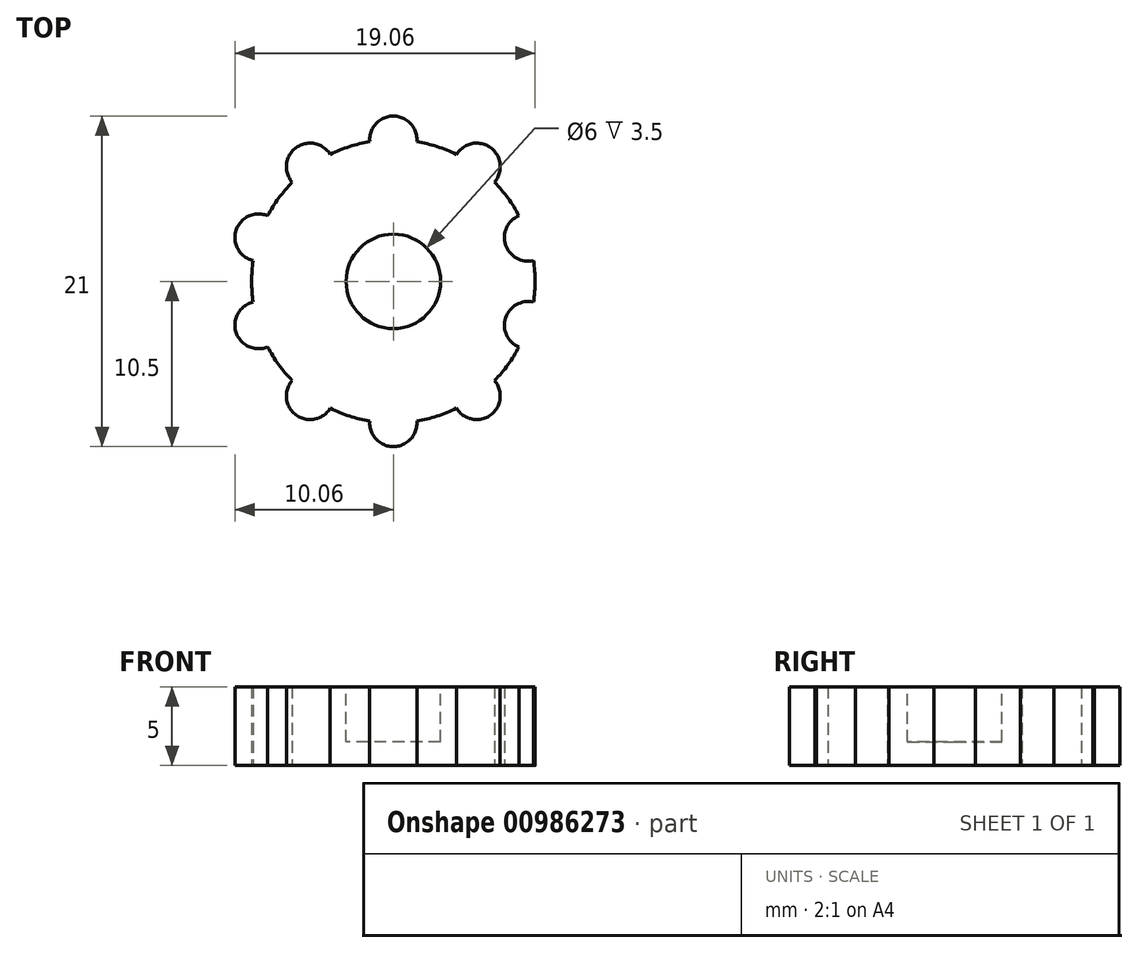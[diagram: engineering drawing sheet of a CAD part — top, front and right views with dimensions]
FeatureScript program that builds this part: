
annotation { "Feature Type Name" : "Feature", "Feature Type Description" : "" }
export const myFeature = defineFeature(function(context is Context, id is Id, definition is map)
    precondition{}
    {
        {
            var Q0;
            Q0=qCreatedBy(makeId("Top.planeOp"),FACE);
            var sketch = newSketch(context, id + "F0", { "sketchPlane" : qUnion([Q0])});
            skCircle(sketch, "E0", {"center": v(0, 0) * mm, "radius": 3 * mm});
            skCircle(sketch, "E1", {"center": v(0, 0) * mm, "radius": 9 * mm});
            skCircle(sketch, "E2", {"center": v(0, 9) * mm, "radius": 1.5 * mm});
            skCircle(sketch, "E3.1.0", {"center": v(-5.3, 7.28) * mm, "radius": 1.5 * mm});
            skCircle(sketch, "E3.2.0", {"center": v(-8.56, 2.78) * mm, "radius": 1.5 * mm});
            skCircle(sketch, "E3.3.0", {"center": v(-8.56, -2.78) * mm, "radius": 1.5 * mm});
            skCircle(sketch, "E3.4.0", {"center": v(-5.3, -7.28) * mm, "radius": 1.5 * mm});
            skCircle(sketch, "E3.5.0", {"center": v(0, -9) * mm, "radius": 1.5 * mm});
            skCircle(sketch, "E3.6.0", {"center": v(5.3, -7.28) * mm, "radius": 1.5 * mm});
            skCircle(sketch, "E3.7.0", {"center": v(8.56, -2.78) * mm, "radius": 1.5 * mm});
            skCircle(sketch, "E3.8.0", {"center": v(8.56, 2.78) * mm, "radius": 1.5 * mm});
            skCircle(sketch, "E3.9.0", {"center": v(5.3, 7.28) * mm, "radius": 1.5 * mm});
            skSolve(sketch);
        }
        {
            var Q0;
            {var subQ0=sQuery(id+"F0.wireOp",EDGE,"E3.1.0");var subQ1=sQuery(id+"F0.wireOp",EDGE,"E1");var subQ2=makeQuery(id+"F0.imprint","INTERSECT",VERTEX,{"disambiguationData":[OD(0.0)],"derivedFrom":[subQ1,subQ0]});Q0=makeQuery(id+"F0.imprint","IMPRINT",FACE,{"disambiguationData":[TD([[makeQuery(id+"F0.imprint","IMPRINT",EDGE,{"disambiguationData":[TD([[subQ2,-1.0]])],"derivedFrom":subQ1}),-1.0]])]});}
            var Q1;
            {var subQ0=sQuery(id+"F0.wireOp",EDGE,"E2");var subQ1=sQuery(id+"F0.wireOp",EDGE,"E1");var subQ2=makeQuery(id+"F0.imprint","INTERSECT",VERTEX,{"disambiguationData":[OD(0.0)],"derivedFrom":[subQ1,subQ0]});Q1=makeQuery(id+"F0.imprint","IMPRINT",FACE,{"disambiguationData":[TD([[makeQuery(id+"F0.imprint","IMPRINT",EDGE,{"disambiguationData":[TD([[subQ2,-1.0]])],"derivedFrom":subQ1}),-1.0]])]});}
            var Q2;
            {var subQ0=sQuery(id+"F0.wireOp",EDGE,"E3.9.0");var subQ1=sQuery(id+"F0.wireOp",EDGE,"E1");var subQ2=makeQuery(id+"F0.imprint","INTERSECT",VERTEX,{"disambiguationData":[OD(0.0)],"derivedFrom":[subQ1,subQ0]});Q2=makeQuery(id+"F0.imprint","IMPRINT",FACE,{"disambiguationData":[TD([[makeQuery(id+"F0.imprint","IMPRINT",EDGE,{"disambiguationData":[TD([[subQ2,-1.0]])],"derivedFrom":subQ1}),-1.0]])]});}
            var Q3;
            {var subQ0=sQuery(id+"F0.wireOp",EDGE,"E3.8.0");var subQ1=sQuery(id+"F0.wireOp",EDGE,"E1");var subQ2=makeQuery(id+"F0.imprint","INTERSECT",VERTEX,{"disambiguationData":[OD(0.0)],"derivedFrom":[subQ1,subQ0]});Q3=makeQuery(id+"F0.imprint","IMPRINT",FACE,{"disambiguationData":[TD([[makeQuery(id+"F0.imprint","IMPRINT",EDGE,{"disambiguationData":[TD([[subQ2,1.0]])],"derivedFrom":subQ1}),-1.0]])]});}
            var Q4;
            {var subQ0=sQuery(id+"F0.wireOp",EDGE,"E3.7.0");var subQ1=sQuery(id+"F0.wireOp",EDGE,"E1");var subQ2=makeQuery(id+"F0.imprint","INTERSECT",VERTEX,{"disambiguationData":[OD(0.0)],"derivedFrom":[subQ1,subQ0]});Q4=makeQuery(id+"F0.imprint","IMPRINT",FACE,{"disambiguationData":[TD([[makeQuery(id+"F0.imprint","IMPRINT",EDGE,{"disambiguationData":[TD([[subQ2,-1.0]])],"derivedFrom":subQ1}),-1.0]])]});}
            var Q5;
            {var subQ0=sQuery(id+"F0.wireOp",EDGE,"E3.6.0");var subQ1=sQuery(id+"F0.wireOp",EDGE,"E1");var subQ2=makeQuery(id+"F0.imprint","INTERSECT",VERTEX,{"disambiguationData":[OD(0.0)],"derivedFrom":[subQ1,subQ0]});Q5=makeQuery(id+"F0.imprint","IMPRINT",FACE,{"disambiguationData":[TD([[makeQuery(id+"F0.imprint","IMPRINT",EDGE,{"disambiguationData":[TD([[subQ2,-1.0]])],"derivedFrom":subQ1}),-1.0]])]});}
            var Q6;
            {var subQ0=sQuery(id+"F0.wireOp",EDGE,"E3.5.0");var subQ1=sQuery(id+"F0.wireOp",EDGE,"E1");var subQ2=makeQuery(id+"F0.imprint","INTERSECT",VERTEX,{"disambiguationData":[OD(0.0)],"derivedFrom":[subQ1,subQ0]});Q6=makeQuery(id+"F0.imprint","IMPRINT",FACE,{"disambiguationData":[TD([[makeQuery(id+"F0.imprint","IMPRINT",EDGE,{"disambiguationData":[TD([[subQ2,-1.0]])],"derivedFrom":subQ1}),-1.0]])]});}
            var Q7;
            {var subQ0=sQuery(id+"F0.wireOp",EDGE,"E3.4.0");var subQ1=sQuery(id+"F0.wireOp",EDGE,"E1");var subQ2=makeQuery(id+"F0.imprint","INTERSECT",VERTEX,{"disambiguationData":[OD(0.0)],"derivedFrom":[subQ1,subQ0]});Q7=makeQuery(id+"F0.imprint","IMPRINT",FACE,{"disambiguationData":[TD([[makeQuery(id+"F0.imprint","IMPRINT",EDGE,{"disambiguationData":[TD([[subQ2,-1.0]])],"derivedFrom":subQ1}),-1.0]])]});}
            var Q8;
            {var subQ0=sQuery(id+"F0.wireOp",EDGE,"E3.3.0");var subQ1=sQuery(id+"F0.wireOp",EDGE,"E1");var subQ2=makeQuery(id+"F0.imprint","INTERSECT",VERTEX,{"disambiguationData":[OD(0.0)],"derivedFrom":[subQ1,subQ0]});Q8=makeQuery(id+"F0.imprint","IMPRINT",FACE,{"disambiguationData":[TD([[makeQuery(id+"F0.imprint","IMPRINT",EDGE,{"disambiguationData":[TD([[subQ2,-1.0]])],"derivedFrom":subQ1}),-1.0]])]});}
            var Q9;
            {var subQ0=sQuery(id+"F0.wireOp",EDGE,"E3.2.0");var subQ1=sQuery(id+"F0.wireOp",EDGE,"E1");var subQ2=makeQuery(id+"F0.imprint","INTERSECT",VERTEX,{"disambiguationData":[OD(0.0)],"derivedFrom":[subQ1,subQ0]});Q9=makeQuery(id+"F0.imprint","IMPRINT",FACE,{"disambiguationData":[TD([[makeQuery(id+"F0.imprint","IMPRINT",EDGE,{"disambiguationData":[TD([[subQ2,-1.0]])],"derivedFrom":subQ1}),-1.0]])]});}
            var Q10;
            Q10=makeQuery(id+"F0.imprint","IMPRINT",FACE,{"disambiguationData":[TD([[makeQuery(id+"F0.imprint","IMPRINT",EDGE,{"derivedFrom":sQuery(id+"F0.wireOp",EDGE,"E0")}),-1.0]])]});
            var Q11;
            {var subQ0=sQuery(id+"F0.wireOp",EDGE,"E3.2.0");var subQ1=sQuery(id+"F0.wireOp",EDGE,"E1");var subQ2=makeQuery(id+"F0.imprint","INTERSECT",VERTEX,{"disambiguationData":[OD(0.0)],"derivedFrom":[subQ1,subQ0]});Q11=makeQuery(id+"F0.imprint","IMPRINT",FACE,{"disambiguationData":[TD([[makeQuery(id+"F0.imprint","IMPRINT",EDGE,{"disambiguationData":[TD([[subQ2,-1.0]])],"derivedFrom":subQ1}),1.0]])]});}
            var Q12;
            {var subQ0=sQuery(id+"F0.wireOp",EDGE,"E3.1.0");var subQ1=sQuery(id+"F0.wireOp",EDGE,"E1");var subQ2=makeQuery(id+"F0.imprint","INTERSECT",VERTEX,{"disambiguationData":[OD(0.0)],"derivedFrom":[subQ1,subQ0]});Q12=makeQuery(id+"F0.imprint","IMPRINT",FACE,{"disambiguationData":[TD([[makeQuery(id+"F0.imprint","IMPRINT",EDGE,{"disambiguationData":[TD([[subQ2,-1.0]])],"derivedFrom":subQ1}),1.0]])]});}
            var Q13;
            {var subQ0=sQuery(id+"F0.wireOp",EDGE,"E2");var subQ1=sQuery(id+"F0.wireOp",EDGE,"E1");var subQ2=makeQuery(id+"F0.imprint","INTERSECT",VERTEX,{"disambiguationData":[OD(0.0)],"derivedFrom":[subQ1,subQ0]});Q13=makeQuery(id+"F0.imprint","IMPRINT",FACE,{"disambiguationData":[TD([[makeQuery(id+"F0.imprint","IMPRINT",EDGE,{"disambiguationData":[TD([[subQ2,-1.0]])],"derivedFrom":subQ1}),1.0]])]});}
            var Q14;
            {var subQ0=sQuery(id+"F0.wireOp",EDGE,"E3.9.0");var subQ1=sQuery(id+"F0.wireOp",EDGE,"E1");var subQ2=makeQuery(id+"F0.imprint","INTERSECT",VERTEX,{"disambiguationData":[OD(0.0)],"derivedFrom":[subQ1,subQ0]});Q14=makeQuery(id+"F0.imprint","IMPRINT",FACE,{"disambiguationData":[TD([[makeQuery(id+"F0.imprint","IMPRINT",EDGE,{"disambiguationData":[TD([[subQ2,-1.0]])],"derivedFrom":subQ1}),1.0]])]});}
            var Q15;
            {var subQ0=sQuery(id+"F0.wireOp",EDGE,"E3.8.0");var subQ1=sQuery(id+"F0.wireOp",EDGE,"E1");var subQ2=makeQuery(id+"F0.imprint","INTERSECT",VERTEX,{"disambiguationData":[OD(0.0)],"derivedFrom":[subQ1,subQ0]});Q15=makeQuery(id+"F0.imprint","IMPRINT",FACE,{"disambiguationData":[TD([[makeQuery(id+"F0.imprint","IMPRINT",EDGE,{"disambiguationData":[TD([[subQ2,1.0]])],"derivedFrom":subQ1}),1.0]])]});}
            var Q16;
            {var subQ0=sQuery(id+"F0.wireOp",EDGE,"E3.7.0");var subQ1=sQuery(id+"F0.wireOp",EDGE,"E1");var subQ2=makeQuery(id+"F0.imprint","INTERSECT",VERTEX,{"disambiguationData":[OD(0.0)],"derivedFrom":[subQ1,subQ0]});Q16=makeQuery(id+"F0.imprint","IMPRINT",FACE,{"disambiguationData":[TD([[makeQuery(id+"F0.imprint","IMPRINT",EDGE,{"disambiguationData":[TD([[subQ2,-1.0]])],"derivedFrom":subQ1}),1.0]])]});}
            var Q17;
            {var subQ0=sQuery(id+"F0.wireOp",EDGE,"E3.6.0");var subQ1=sQuery(id+"F0.wireOp",EDGE,"E1");var subQ2=makeQuery(id+"F0.imprint","INTERSECT",VERTEX,{"disambiguationData":[OD(0.0)],"derivedFrom":[subQ1,subQ0]});Q17=makeQuery(id+"F0.imprint","IMPRINT",FACE,{"disambiguationData":[TD([[makeQuery(id+"F0.imprint","IMPRINT",EDGE,{"disambiguationData":[TD([[subQ2,-1.0]])],"derivedFrom":subQ1}),1.0]])]});}
            var Q18;
            {var subQ0=sQuery(id+"F0.wireOp",EDGE,"E3.5.0");var subQ1=sQuery(id+"F0.wireOp",EDGE,"E1");var subQ2=makeQuery(id+"F0.imprint","INTERSECT",VERTEX,{"disambiguationData":[OD(0.0)],"derivedFrom":[subQ1,subQ0]});Q18=makeQuery(id+"F0.imprint","IMPRINT",FACE,{"disambiguationData":[TD([[makeQuery(id+"F0.imprint","IMPRINT",EDGE,{"disambiguationData":[TD([[subQ2,-1.0]])],"derivedFrom":subQ1}),1.0]])]});}
            var Q19;
            Q19=makeQuery(id+"F0.imprint","IMPRINT",FACE,{"disambiguationData":[TD([[makeQuery(id+"F0.imprint","IMPRINT",EDGE,{"derivedFrom":sQuery(id+"F0.wireOp",EDGE,"E0")}),1.0]])]});
            var Q20;
            {var subQ0=sQuery(id+"F0.wireOp",EDGE,"E3.4.0");var subQ1=sQuery(id+"F0.wireOp",EDGE,"E1");var subQ2=makeQuery(id+"F0.imprint","INTERSECT",VERTEX,{"disambiguationData":[OD(0.0)],"derivedFrom":[subQ1,subQ0]});Q20=makeQuery(id+"F0.imprint","IMPRINT",FACE,{"disambiguationData":[TD([[makeQuery(id+"F0.imprint","IMPRINT",EDGE,{"disambiguationData":[TD([[subQ2,-1.0]])],"derivedFrom":subQ1}),1.0]])]});}
            var Q21;
            {var subQ0=sQuery(id+"F0.wireOp",EDGE,"E3.3.0");var subQ1=sQuery(id+"F0.wireOp",EDGE,"E1");var subQ2=makeQuery(id+"F0.imprint","INTERSECT",VERTEX,{"disambiguationData":[OD(0.0)],"derivedFrom":[subQ1,subQ0]});Q21=makeQuery(id+"F0.imprint","IMPRINT",FACE,{"disambiguationData":[TD([[makeQuery(id+"F0.imprint","IMPRINT",EDGE,{"disambiguationData":[TD([[subQ2,-1.0]])],"derivedFrom":subQ1}),1.0]])]});}
            extrude(context, id + "F1", {"entities" : qUnion([Q0, Q1, Q2, Q3, Q4, Q5, Q6, Q7, Q8, Q9, Q10, Q11, Q12, Q13, Q14, Q15, Q16, Q17, Q18, Q19, Q20, Q21]), "depth" : 5 * mm, "offsetDistance" : 25 * mm});
        }
        {
            var Q0;
            Q0=makeQuery(id+"F1.opExtrude","CAP_FACE",FACE,{"disambiguationData":[OSD([sQuery(id+"F0.wireOp",EDGE,"E1"),sQuery(id+"F0.wireOp",EDGE,"E2"),sQuery(id+"F0.wireOp",EDGE,"E3.1.0"),sQuery(id+"F0.wireOp",EDGE,"E3.2.0"),sQuery(id+"F0.wireOp",EDGE,"E3.3.0"),sQuery(id+"F0.wireOp",EDGE,"E3.4.0"),sQuery(id+"F0.wireOp",EDGE,"E3.5.0"),sQuery(id+"F0.wireOp",EDGE,"E3.6.0"),sQuery(id+"F0.wireOp",EDGE,"E3.7.0"),sQuery(id+"F0.wireOp",EDGE,"E3.8.0"),sQuery(id+"F0.wireOp",EDGE,"E3.9.0")])],"isStart":false});
            var sketch = newSketch(context, id + "F2", { "sketchPlane" : qUnion([Q0])});
            skCircle(sketch, "E4", {"center": v(0, 0) * mm, "radius": 3 * mm});
            skSolve(sketch);
        }
        {
            var Q0;
            Q0=makeQuery(id+"F2.imprint","IMPRINT",FACE,{"disambiguationData":[TD([[makeQuery(id+"F2.imprint","IMPRINT",EDGE,{"derivedFrom":sQuery(id+"F2.wireOp",EDGE,"E4")}),1.0]])]});
            extrude(context, id + "F3", {"entities" : qUnion([Q0]), "operationType" : NewBodyOperationType.REMOVE, "oppositeDirection" : true, "depth" : 3.5 * mm, "offsetDistance" : 25 * mm});
        }
    });
